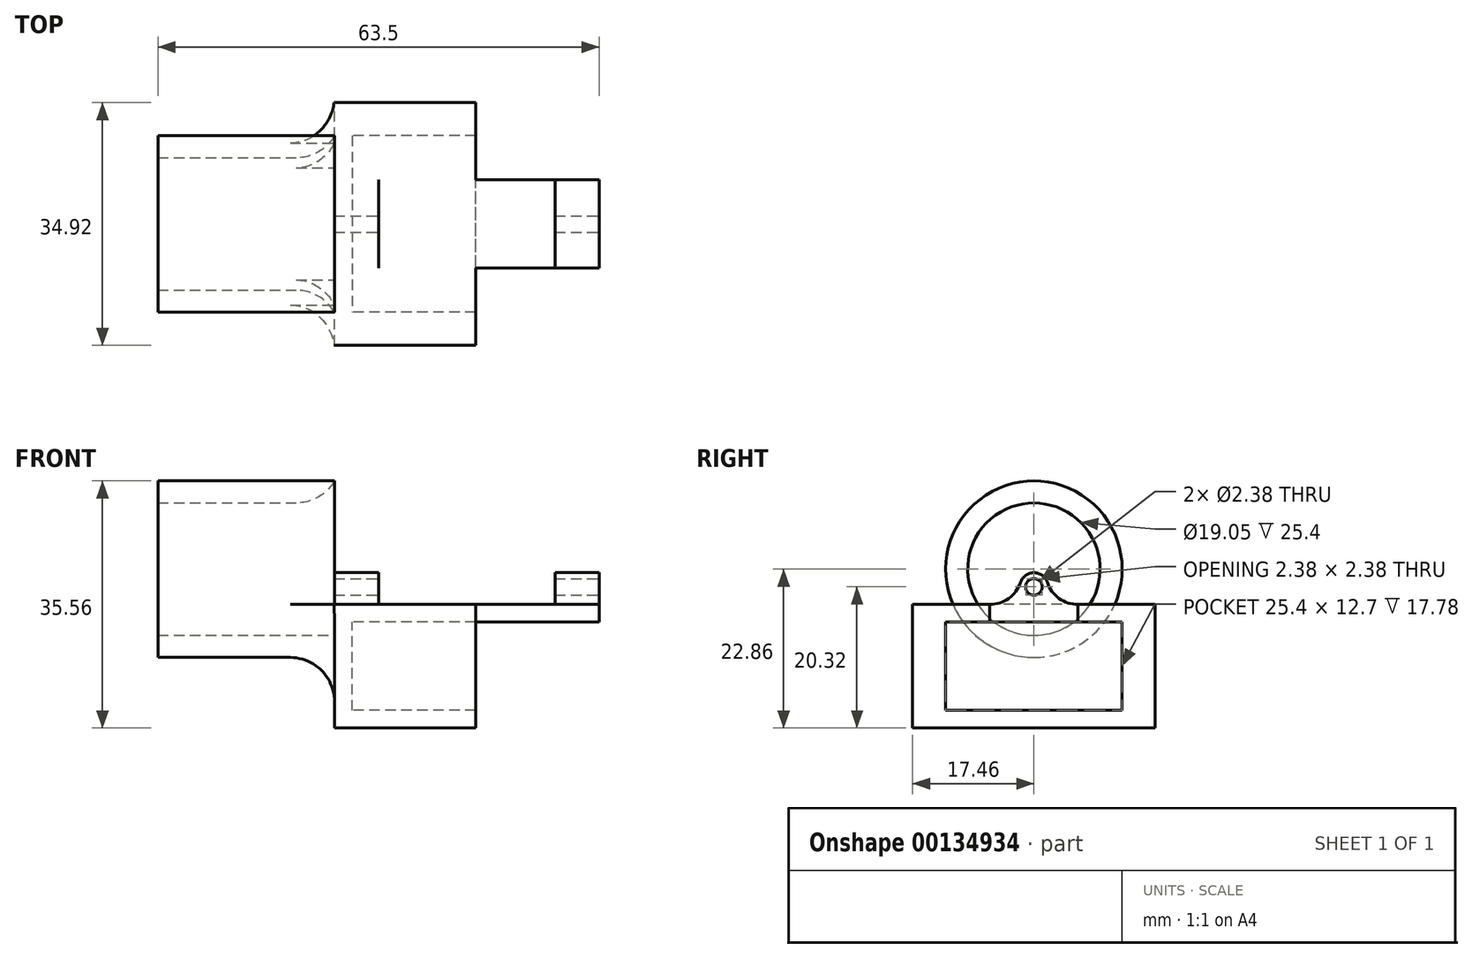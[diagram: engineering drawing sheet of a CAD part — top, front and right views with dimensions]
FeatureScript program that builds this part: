
annotation { "Feature Type Name" : "Feature", "Feature Type Description" : "" }
export const myFeature = defineFeature(function(context is Context, id is Id, definition is map)
    precondition{}
    {
        {
            var Q0;
            Q0=qCreatedBy(makeId("Right.planeOp"),FACE);
            var sketch = newSketch(context, id + "F0", { "sketchPlane" : qUnion([Q0])});
            skCircle(sketch, "E0", {"center": v(0, 0) * mm, "radius": 12.7 * mm});
            skCircle(sketch, "E1", {"center": v(0, 0) * mm, "radius": 9.53 * mm});
            skSolve(sketch);
        }
        {
            var Q0;
            Q0 = qSketchRegion(id + "F0", true);
            extrude(context, id + "F1", {"entities" : qUnion([Q0]), "oppositeDirection" : true, "depth" : 25.4 * mm});
        }
        {
            var Q0;
            Q0=qCreatedBy(makeId("Right.planeOp"),FACE);
            var sketch = newSketch(context, id + "F2", { "sketchPlane" : qUnion([Q0])});
            skLineSegment(sketch, "E2.bottom", {"start": v(-12.7, -7.62) * mm, "end": v(12.7, -7.62) * mm});
            skLineSegment(sketch, "E2.top", {"start": v(-12.7, -20.32) * mm, "end": v(12.7, -20.32) * mm});
            skLineSegment(sketch, "E2.left", {"start": v(-12.7, -7.62) * mm, "end": v(-12.7, -20.32) * mm});
            skLineSegment(sketch, "E2.right", {"start": v(12.7, -7.62) * mm, "end": v(12.7, -20.32) * mm});
            skLineSegment(sketch, "E3.bottom", {"start": v(-17.46, -5.08) * mm, "end": v(17.46, -5.08) * mm});
            skLineSegment(sketch, "E3.top", {"start": v(-17.46, -22.86) * mm, "end": v(17.46, -22.86) * mm});
            skLineSegment(sketch, "E3.left", {"start": v(-17.46, -5.08) * mm, "end": v(-17.46, -22.86) * mm});
            skLineSegment(sketch, "E3.right", {"start": v(17.46, -5.08) * mm, "end": v(17.46, -22.86) * mm});
            skLineSegment(sketch, "E4", {"start": v(0, 0) * mm, "end": v(0, -7.62) * mm, "construction": true});
            skSolve(sketch);
        }
        {
            var Q0;
            Q0=makeQuery(id+"F2.imprint","IMPRINT",FACE,{"disambiguationData":[TD([[makeQuery(id+"F2.imprint","IMPRINT",EDGE,{"derivedFrom":sQuery(id+"F2.wireOp",EDGE,"E2.bottom")}),1.0]])]});
            var Q1;
            Q1=makeQuery(id+"F2.imprint","IMPRINT",FACE,{"disambiguationData":[TD([[makeQuery(id+"F2.imprint","IMPRINT",EDGE,{"derivedFrom":sQuery(id+"F2.wireOp",EDGE,"E2.bottom")}),-1.0]])]});
            extrude(context, id + "F3", {"entities" : qUnion([Q0, Q1]), "operationType" : NewBodyOperationType.ADD, "depth" : 2.54 * mm});
        }
        {
            var Q0;
            Q0 = qSketchRegion(id + "F2", true);
            extrude(context, id + "F4", {"entities" : qUnion([Q0]), "operationType" : NewBodyOperationType.ADD, "depth" : 20.32 * mm});
        }
        {
            var Q0;
            {var subQ0=sQuery(id+"F0.wireOp",EDGE,"E1");Q0=makeQuery(id+"F3.boolean.opBoolean","SPLIT",EDGE,{"disambiguationData":[topologyDisambiguationEdgeConnected([makeQuery(id+"F3.opExtrude","CAP_FACE",FACE,{"disambiguationData":[OSD([sQuery(id+"F2.wireOp",EDGE,"E3.bottom"),sQuery(id+"F2.wireOp",EDGE,"E3.top"),sQuery(id+"F2.wireOp",EDGE,"E3.left"),sQuery(id+"F2.wireOp",EDGE,"E3.right")])],"isStart":true})])],"derivedFrom":makeQuery(id+"F1.opExtrude","CAP_EDGE",EDGE,{"disambiguationData":[OSD([subQ0])],"isStart":true})});}
            var Q1;
            {var subQ0=sQuery(id+"F0.wireOp",EDGE,"E0");Q1=makeQuery(id+"F3.boolean.opBoolean","SPLIT",EDGE,{"disambiguationData":[topologyDisambiguationEdgeConnected([makeQuery(id+"F3.opExtrude","CAP_FACE",FACE,{"disambiguationData":[OSD([sQuery(id+"F2.wireOp",EDGE,"E3.bottom"),sQuery(id+"F2.wireOp",EDGE,"E3.top"),sQuery(id+"F2.wireOp",EDGE,"E3.left"),sQuery(id+"F2.wireOp",EDGE,"E3.right")])],"isStart":true})])],"derivedFrom":makeQuery(id+"F1.opExtrude","CAP_EDGE",EDGE,{"disambiguationData":[OSD([subQ0])],"isStart":true})});}
            fillet(context, id + "F5", {"entities" : qUnion([Q0, Q1]), "radius" : 6.35 * mm, "tangentPropagation" : true, "allowEdgeOverflow" : false});
        }
        {
            var Q0;
            Q0=makeQuery(id+"F4.opExtrude","CAP_FACE",FACE,{"disambiguationData":[OSD([sQuery(id+"F2.wireOp",EDGE,"E2.bottom"),sQuery(id+"F2.wireOp",EDGE,"E2.top"),sQuery(id+"F2.wireOp",EDGE,"E2.left"),sQuery(id+"F2.wireOp",EDGE,"E2.right"),sQuery(id+"F2.wireOp",EDGE,"E3.bottom"),sQuery(id+"F2.wireOp",EDGE,"E3.top"),sQuery(id+"F2.wireOp",EDGE,"E3.left"),sQuery(id+"F2.wireOp",EDGE,"E3.right")])],"isStart":false});
            var sketch = newSketch(context, id + "F6", { "sketchPlane" : qUnion([Q0])});
            skLineSegment(sketch, "E5.bottom", {"start": v(-17.46, -5.08) * mm, "end": v(6.35, -5.08) * mm});
            skLineSegment(sketch, "E5.top", {"start": v(-6.35, -7.62) * mm, "end": v(6.35, -7.62) * mm});
            skLineSegment(sketch, "E5.left", {"start": v(-6.35, -5.08) * mm, "end": v(-6.35, -7.62) * mm});
            skLineSegment(sketch, "E5.right", {"start": v(6.35, -5.08) * mm, "end": v(6.35, -7.62) * mm});
            skLineSegment(sketch, "E6", {"start": v(0, -7.62) * mm, "end": v(0, -5.08) * mm, "construction": true});
            skSolve(sketch);
        }
        {
            var Q0;
            Q0 = qSketchRegion(id + "F6", true);
            extrude(context, id + "F7", {"entities" : qUnion([Q0]), "operationType" : NewBodyOperationType.ADD, "depth" : 17.78 * mm});
        }
        {
            var Q0;
            Q0=makeQuery(id+"F7.opExtrude","CAP_FACE",FACE,{"disambiguationData":[OSD([sQuery(id+"F6.wireOp",EDGE,"E5.bottom"),sQuery(id+"F6.wireOp",EDGE,"E5.top"),sQuery(id+"F6.wireOp",EDGE,"E5.left"),sQuery(id+"F6.wireOp",EDGE,"E5.right")])],"isStart":false});
            var sketch = newSketch(context, id + "F8", { "sketchPlane" : qUnion([Q0])});
            skCircle(sketch, "E7", {"center": v(0, -2.54) * mm, "radius": 1.2 * mm});
            skArc(sketch, "E8", {"start": v(-1.93, -1.9) * mm, "mid": v(0, -0.5) * mm, "end": v(1.93, -1.9) * mm});
            skArc(sketch, "E9", {"start": v(1.93, -1.9) * mm, "mid": v(3.62, -4.2) * mm, "end": v(6.35, -5.08) * mm});
            skArc(sketch, "E10", {"start": v(-1.93, -1.9) * mm, "mid": v(-3.62, -4.2) * mm, "end": v(-6.35, -5.08) * mm});
            skSolve(sketch);
        }
        {
            var Q0;
            Q0=makeQuery(id+"F8.imprint","IMPRINT",FACE,{"disambiguationData":[TD([[makeQuery(id+"F8.imprint","IMPRINT",EDGE,{"derivedFrom":sQuery(id+"F8.wireOp",EDGE,"E7")}),-1.0]])]});
            extrude(context, id + "F9", {"entities" : qUnion([Q0]), "operationType" : NewBodyOperationType.ADD, "oppositeDirection" : true, "depth" : 38.1 * mm});
        }
        {
            var Q0;
            Q0=qCreatedBy(makeId("Front.planeOp"),FACE);
            var sketch = newSketch(context, id + "F10", { "sketchPlane" : qUnion([Q0])});
            skLineSegment(sketch, "E11.bottom", {"start": v(6.35, 0) * mm, "end": v(31.75, 0) * mm});
            skLineSegment(sketch, "E11.top", {"start": v(6.35, -5.08) * mm, "end": v(31.75, -5.08) * mm});
            skLineSegment(sketch, "E11.left", {"start": v(6.35, 0) * mm, "end": v(6.35, -5.08) * mm});
            skLineSegment(sketch, "E11.right", {"start": v(31.75, 0) * mm, "end": v(31.75, -5.08) * mm});
            skSolve(sketch);
        }
        {
            var Q0;
            Q0 = qSketchRegion(id + "F10", true);
            extrude(context, id + "F11", {"entities" : qUnion([Q0]), "operationType" : NewBodyOperationType.REMOVE, "endBound" : BoundingType.SYMMETRIC, "oppositeDirection" : true, "depth" : 25.4 * mm});
        }
    });
